# Revit family: Sanitary_Accessories_Svedholm_Slits-floor-stand
name_source: partatom
category: Furniture
revit_build: Autodesk Revit 2018 (Build: 20190510_1515(x64)
units: mm (PartAtom-declared; Revit-internal decimal feet)

## family parameters
Always vertical = No
Cut with Voids When Loaded = No
OmniClass Number = 23.21.11.00
OmniClass Title = Commercial Furniture
Room Calculation Point = No
Shared = No
Work Plane-Based = Yes

## types (2) — shared parameters
BIMobject category = Accessories
BIMobject category code = sanitary-accessories1
BIMobject main category = Sanitary
BIMobject main category code = sanitary
Brand url = https://www.svedholm.se
Default Elevation = 1219.2 mm  [stored 4 ft]
Description = Floor stand made of powder coated steel. Adapted for Slits alcogel/soap dispenser.
Design country = Sweden
Edition number = 1
Frame material = Svedholm - Plastic - White
IFC Classification = Object
Manufacturer = Svedholm
Manufacturer country = Sweden
Manufacturer name = Svedholm
Material main = Powder coated steel
Model = Floor stand
OmniClass Code = 23-21 11 00
OmniClass Description = Commercial Furniture
Product Guid = a2b3fc05-037c-445d-85b4-1dbb5fa160e2
Product SKU = Slits-floor-stand
Product data url = https://bimobject.com
Product family = Slits
Product group = Stand
Product name = Slits floor stand
Product url = https://www.svedholm.se
QR code = http://bimobject.com
URL = https://www.svedholm.se
Uniclass 2015 Code = Zz_30_60
Uniclass 2015 Name = Objects

## per-type parameters (varying)
| type | Hood visibility |
| ART - (410.600.071) Sign board - (yes) | Yes |
| ART - (410.600.070) Sign board - (no) | No |

note: [stored X ft] marks values corroborated as IEEE doubles in the binary element streams (Revit-internal decimal feet)

## geometry (parser evidence)
native form markers: Sweep x3
no freeform markers — native parametric forms only
